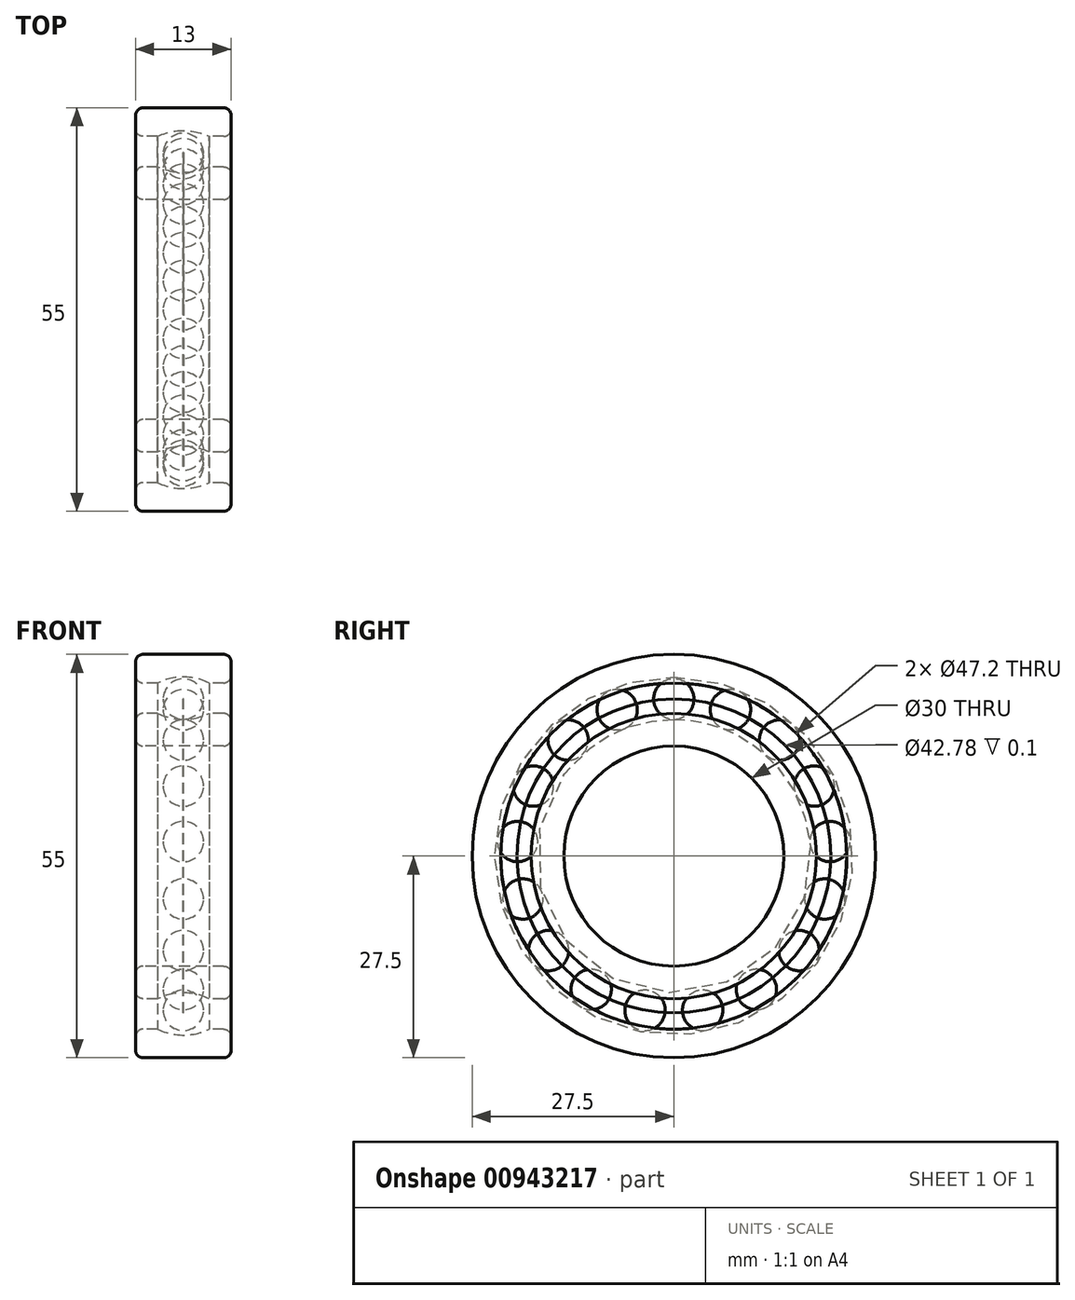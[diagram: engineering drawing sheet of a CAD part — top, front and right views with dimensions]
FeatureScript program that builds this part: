
annotation { "Feature Type Name" : "Feature", "Feature Type Description" : "" }
export const myFeature = defineFeature(function(context is Context, id is Id, definition is map)
    precondition{}
    {
        {
            var Q0;
            Q0=qCreatedBy(makeId("Front.planeOp"),FACE);
            var sketch = newSketch(context, id + "F0", { "sketchPlane" : qUnion([Q0])});
            skLineSegment(sketch, "E0", {"start": v(-6.5, 0) * mm, "end": v(6.5, 0) * mm, "construction": true});
            skLineSegment(sketch, "E1", {"start": v(-6.5, 0) * mm, "end": v(-6.5, 15) * mm, "construction": true});
            skLineSegment(sketch, "E2.MirrorCS", {"start": v(6.5, 0) * mm, "end": v(6.5, 15) * mm, "construction": true});
            skLineSegment(sketch, "E3", {"start": v(-5.5, 15) * mm, "end": v(5.5, 15) * mm});
            skLineSegment(sketch, "E4", {"start": v(-6.5, 16) * mm, "end": v(-6.5, 18.45) * mm});
            skLineSegment(sketch, "E5.MirrorCS", {"start": v(6.5, 16) * mm, "end": v(6.5, 18.45) * mm});
            skLineSegment(sketch, "E6", {"start": v(-5.5, 19.45) * mm, "end": v(-3.5, 19.45) * mm});
            skLineSegment(sketch, "E7.MirrorCS", {"start": v(5.5, 19.45) * mm, "end": v(3.5, 19.45) * mm});
            skArc(sketch, "E8", {"start": v(-3.5, 19.45) * mm, "mid": v(0, 18.64) * mm, "end": v(3.5, 19.45) * mm});
            skLineSegment(sketch, "E9", {"start": v(-6.5, 0) * mm, "end": v(-6.5, 23.6) * mm, "construction": true});
            skLineSegment(sketch, "E10", {"start": v(-6.5, 24.6) * mm, "end": v(-6.5, 26.5) * mm});
            skLineSegment(sketch, "E11", {"start": v(-5.5, 27.5) * mm, "end": v(0, 27.5) * mm});
            skLineSegment(sketch, "E12.MirrorCS", {"start": v(5.5, 27.5) * mm, "end": v(0, 27.5) * mm});
            skLineSegment(sketch, "E13.MirrorCS", {"start": v(6.5, 24.6) * mm, "end": v(6.5, 26.5) * mm});
            skLineSegment(sketch, "E14", {"start": v(-5.5, 23.6) * mm, "end": v(-3.5, 23.6) * mm});
            skLineSegment(sketch, "E15.MirrorCS", {"start": v(5.5, 23.6) * mm, "end": v(3.5, 23.6) * mm});
            skArc(sketch, "E16", {"start": v(3.5, 23.6) * mm, "mid": v(0, 24.4) * mm, "end": v(-3.5, 23.6) * mm});
            skPoint(sketch, "E17.visualSharp", {"position": v(6.5, 27.5) * mm});
            skArc(sketch, "E17.filletArc", {"start": v(6.5, 26.5) * mm, "mid": v(6.2, 27.2) * mm, "end": v(5.5, 27.5) * mm});
            skPoint(sketch, "E18.visualSharp", {"position": v(-6.5, 27.5) * mm});
            skArc(sketch, "E18.filletArc", {"start": v(-5.5, 27.5) * mm, "mid": v(-6.2, 27.2) * mm, "end": v(-6.5, 26.5) * mm});
            skPoint(sketch, "E19.visualSharp", {"position": v(-6.5, 15) * mm});
            skArc(sketch, "E19.filletArc", {"start": v(-6.5, 16) * mm, "mid": v(-6.2, 15.3) * mm, "end": v(-5.5, 15) * mm});
            skPoint(sketch, "E20.visualSharp", {"position": v(6.5, 15) * mm});
            skArc(sketch, "E20.filletArc", {"start": v(5.5, 15) * mm, "mid": v(6.2, 15.3) * mm, "end": v(6.5, 16) * mm});
            skPoint(sketch, "E21.visualSharp", {"position": v(-6.5, 23.6) * mm});
            skArc(sketch, "E21.filletArc", {"start": v(-6.5, 24.6) * mm, "mid": v(-6.2, 23.9) * mm, "end": v(-5.5, 23.6) * mm});
            skPoint(sketch, "E22.visualSharp", {"position": v(-6.5, 19.45) * mm});
            skArc(sketch, "E22.filletArc", {"start": v(-5.5, 19.45) * mm, "mid": v(-6.2, 19.16) * mm, "end": v(-6.5, 18.45) * mm});
            skPoint(sketch, "E23.visualSharp", {"position": v(6.5, 19.45) * mm});
            skArc(sketch, "E23.filletArc", {"start": v(6.5, 18.45) * mm, "mid": v(6.2, 19.16) * mm, "end": v(5.5, 19.45) * mm});
            skPoint(sketch, "E24.visualSharp", {"position": v(6.5, 23.6) * mm});
            skArc(sketch, "E24.filletArc", {"start": v(5.5, 23.6) * mm, "mid": v(6.2, 23.9) * mm, "end": v(6.5, 24.6) * mm});
            skSolve(sketch);
        }
        {
            var Q0;
            Q0=makeQuery(id+"F0.imprint","IMPRINT",FACE,{"disambiguationData":[TD([[makeQuery(id+"F0.imprint","IMPRINT",EDGE,{"derivedFrom":sQuery(id+"F0.wireOp",EDGE,"E10")}),-1.0]])]});
            var Q1;
            Q1=makeQuery(id+"F0.imprint","IMPRINT",FACE,{"disambiguationData":[TD([[makeQuery(id+"F0.imprint","IMPRINT",EDGE,{"derivedFrom":sQuery(id+"F0.wireOp",EDGE,"E3")}),1.0]])]});
            var Q2;
            Q2=sQuery(id+"F0.wireOp",EDGE,"E0");
            revolve(context, id + "F1", {"surfaceOperationType" : NewSurfaceOperationType.NEW, "entities" : qUnion([Q0, Q1]), "axis" : qUnion([Q2]), "revolveType" : RevolveType.FULL});
        }
        {
            var Q0;
            Q0=qCreatedBy(makeId("Front.planeOp"),FACE);
            var sketch = newSketch(context, id + "F2", { "sketchPlane" : qUnion([Q0])});
            skArc(sketch, "E25", {"start": v(2.75, 21.4) * mm, "mid": v(0, 24.14) * mm, "end": v(-2.75, 21.4) * mm});
            skLineSegment(sketch, "E26", {"start": v(0, 21.4) * mm, "end": v(3.74, 21.4) * mm, "construction": true});
            skLineSegment(sketch, "E27", {"start": v(0, 21.4) * mm, "end": v(0, 23.25) * mm, "construction": true});
            skLineSegment(sketch, "E28.MirrorCS", {"start": v(0, 21.4) * mm, "end": v(-3.74, 21.4) * mm, "construction": true});
            skLineSegment(sketch, "E29", {"start": v(-2.75, 21.4) * mm, "end": v(2.75, 21.4) * mm});
            skSolve(sketch);
        }
        {
            var Q0;
            Q0=qSketchRegion(id+"F2",true);
            var Q1;
            Q1=sQuery(id+"F2.wireOp",EDGE,"E28.MirrorCS");
            revolve(context, id + "F3", {"surfaceOperationType" : NewSurfaceOperationType.NEW, "entities" : qUnion([Q0]), "axis" : qUnion([Q1]), "revolveType" : RevolveType.FULL});
        }
        {
            var Q0;
            Q0=qCreatedBy(makeId("Top.planeOp"),FACE);
            var sketch = newSketch(context, id + "F4", { "sketchPlane" : qUnion([Q0])});
            skLineSegment(sketch, "E30", {"start": v(0, 0) * mm, "end": v(16.63, 0) * mm, "construction": true});
            skSolve(sketch);
        }
        {
            var Q0;
            Q0=makeQuery(id+"F3.opRevolve","SWEPT_BODY",BODY,{"disambiguationData":[OSD([sQuery(id+"F2.wireOp",EDGE,"E25"),sQuery(id+"F2.wireOp",EDGE,"E29")])]});
            var Q1;
            Q1=sQuery(id+"F4.wireOp",EDGE,"E30");
            circularPattern(context, id + "F5", {"entities" : qUnion([Q0]), "axis" : qUnion([Q1]), "angle" : 360 * degree, "instanceCount" : 17, "equalSpace" : true});
        }
        {
            var Q0;
            Q0=qCreatedBy(makeId("Right.planeOp"),FACE);
            var sketch = newSketch(context, id + "F6", { "sketchPlane" : qUnion([Q0])});
            skCircle(sketch, "E31", {"center": v(0, 0) * mm, "radius": 21.4 * mm});
            skSolve(sketch);
        }
        {
            var Q0;
            Q0=qSketchRegion(id+"F6",true);
            extrude(context, id + "F7", {"entities" : qUnion([Q0]), "depth" : 0.1 * mm, "offsetDistance" : 25 * mm, "symmetric" : true});
        }
    });
